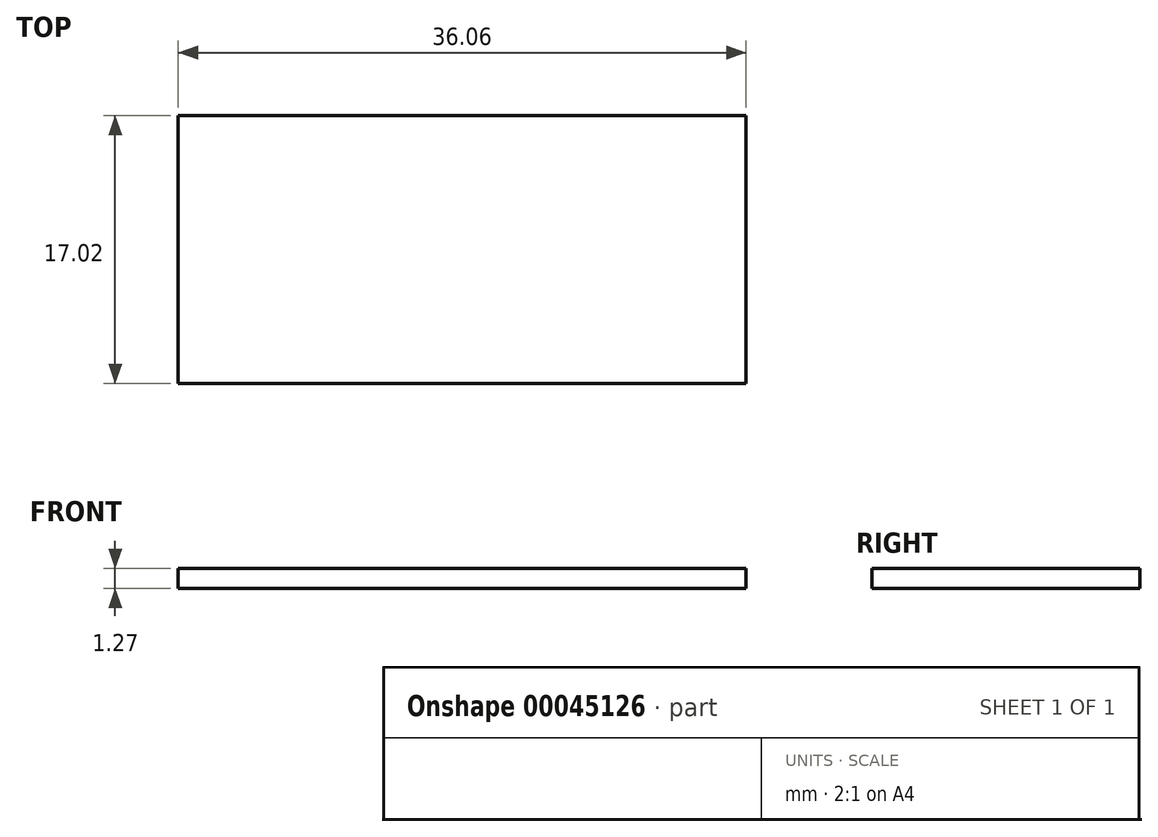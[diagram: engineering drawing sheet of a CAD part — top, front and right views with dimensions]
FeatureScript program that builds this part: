
annotation { "Feature Type Name" : "Feature", "Feature Type Description" : "" }
export const myFeature = defineFeature(function(context is Context, id is Id, definition is map)
    precondition{}
    {
        {
            var Q0;
            Q0=qCreatedBy(makeId("Top.planeOp"),FACE);
            var sketch = newSketch(context, id + "F0", { "sketchPlane" : qUnion([Q0])});
            skLineSegment(sketch, "E0.rect.bottom", {"start": v(18.03, 8.5) * mm, "end": v(-18.03, 8.5) * mm});
            skLineSegment(sketch, "E0.rect.top", {"start": v(18.03, -8.5) * mm, "end": v(-18.03, -8.5) * mm});
            skLineSegment(sketch, "E0.rect.left", {"start": v(18.03, 8.5) * mm, "end": v(18.03, -8.5) * mm});
            skLineSegment(sketch, "E0.rect.right", {"start": v(-18.03, 8.5) * mm, "end": v(-18.03, -8.5) * mm});
            skPoint(sketch, "E0.rect.middle", {"position": v(0, 0) * mm});
            skSolve(sketch);
        }
        {
            var Q0;
            Q0=makeQuery(id+"F0.imprint","IMPRINT",FACE,{"disambiguationData":[TD([[makeQuery(id+"F0.imprint","IMPRINT",EDGE,{"derivedFrom":sQuery(id+"F0.wireOp",EDGE,"E0.rect.bottom")}),1.0]])]});
            extrude(context, id + "F1", {"entities" : qUnion([Q0]), "depth" : 1.27 * mm});
        }
    });
